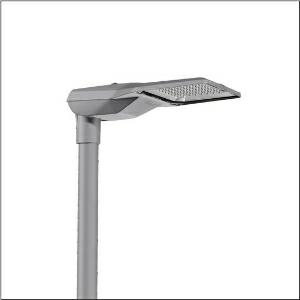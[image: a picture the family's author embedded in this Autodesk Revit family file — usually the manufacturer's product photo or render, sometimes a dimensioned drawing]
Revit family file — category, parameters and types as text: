
# Revit family: streetlight_sl_21_midi___st0_5a_5xe3b33s08mb_18c2
name_source: partatom
category: Lighting Fixtures
units: mm (PartAtom-declared; Revit-internal decimal feet)

## family parameters
Cut with Voids When Loaded = No
Host = Face
Light Source = No
Part Type = Normal
Room Calculation Point = No
Round Connector Dimension = Use Diameter
Shared = No

## types (1)
- --- (1 x LED, 18270 lm, 136 W, 3000K)
    Apparent Load = 136 VA
    CIE Flux Codes = 41 75 97 100 100
    Color Rendering = 70
    Color Temperature = 3000K
    Default Elevation = 1800 mm
    Description = Streetlight SL 21 midi, mast luminaire, primary light control with lens, of PMMA, primary optical cover: cover, of toughened safety glass, transparent, light distribution: ST0.5a, light emission: direct distribution, primary light characteristic: asymmetric, installation type: side-entry, post-top, LED, High Power LED, rated luminous flux: 18.270lm, luminous efficacy: 134lm/W, light colour: 730, colour temperature: 3000K, control gear: D4i, control: overheat protection, constant luminous flux control, time-dependent luminous flux control, flexible luminous flux parameterisation, pre-setting: logarithmic dimming characteristic, mains connection: 230..240V, AC, 50/60Hz, start of lifetime: 136W, end of service life: 142W, reduction: 61W, luminaire housing, of diecast aluminium, powder-coated, Siteco® metallic grey (DB 702S), corrosivity category C5 mid according to DIN EN ISO 12944, please order mast flange separately, inclination adjustable: 0°, 5°, 10°, 15°, sealing non-destructively replaceable, multi-level sealing system, length: 644mm, width: 335mm, height: 110mm, mast flange for spigot size: 42mm (side-entry): 5XC10008XM4, 60/48mm (side-entry/post-top): 5XC10108XM2, 76/60mm (side-entry/post-top): 5XC10108XM1, mounting height: 4..8m, Smart Interface above, protection rating (complete): IP66, insulation class (complete): insulation class II (safety insulation), certification: CE, ENEC, ENEC+, VDE, impact resistance: IK10, permissible operating ambient temperature for outdoor applications: -40..+50°C, standard-compliant lighting for roads and squares, packaging unit: 1 piece

Light Distribution: ST0.5a
    Height = 111 mm
    Lamp = 1 x LED
    Lamp Light Flux = 18270 lm
    Lamp Power = 136 W
    Lamp count = 1
    Length = 644 mm
    Luminous efficacy = 134 lm/W
    Manufacturer = Siteco
    ModVariant = No
    Model = 5XE3B33S08MB
    Number of Poles = 1
    OnlyDefault = Yes
    Power Factor = 1
    Product Name = Streetlight SL 21 midi | ST0.5a
    Product group = mast luminaire | pylon top
    ProductGroupID = 6100
    Protection Class = Protection class II
    Protection Degree = IP 66
    RLX_Detail_Level = 1
    RLX_Emergency_Light_Flux = 0 lm
    RLX_Emergency_Type = 0
    RLX_Emergency_Type_DB = No
    RlxData = <blob elided: 37925 chars, md5=d7c569d8>
    Socket = socket
    Standby Power = 0 W
    System Light Flux = 18270 lm
    System Power = 136 W
    Type Comments = factory setting: luminous flux: 100 % | dim-lin: 254 | 695 mA
    Type Image = l_1004302.jpg
    URL = http://relux.com
    VarID = @adj_213021
    Voltage = 0 V
    Weight = 0.00 kg
    Width = 336 mm

## geometry (parser evidence)
native form markers: Blend x4, Sweep x11
no freeform markers — native parametric forms only
